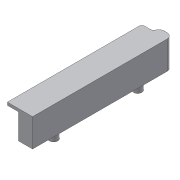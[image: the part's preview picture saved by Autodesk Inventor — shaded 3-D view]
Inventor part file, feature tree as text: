
AUTODESK INVENTOR PART (.ipt)
format: ipt  version: 2013 (Build 170138000, 138)  size: 107,520 bytes
history: native  units: mm
features: extrude x3, sketch x3, fillet x1, mirror x1
ambient origin geometry x8: Origin, YZ Plane, XZ Plane, XY Plane, X Axis, Y Axis, Z Axis, Center Point
bodies: Volumenkörper1 (feature_tree)
feature tree (8):
  extrude  "Extrusion1"  Depth=50.0mm
  extrude  "Extrusion2"  Depth=10.0mm TaperAngle=0.0deg
  fillet  "Rundung1"  Radius=1.0mm
  mirror  "Spiegeln1"
  extrude  "Extrusion3"  Depth=1.0mm
  sketch  "Skizze1"  dims[d0=5.0mm d1=50.0mm]
  sketch  "Skizze2"  dims[d2=2.0mm d3=10.0mm d4=0.0mm d5=1.0mm]
  sketch  "Skizze3"  dims[d6=4.0mm d7=0.0mm d8=1.0mm d9=3.0mm d10=3.0mm d11=2.5mm d12=2.5mm d13=10.0mm d14=40.0mm d15=3.0mm d16=0.0mm]
